# Revit family: Skylight_Velux-Sun_Tunnels-TMC-14in
name_source: partatom
category: Specialty Equipment
revit_build: Autodesk Revit 2015 (Build: 20140606_1530(x64)
units: mm (PartAtom-declared; Revit-internal decimal feet)

## types (1)
- TMC - 14"
    Assembly Code = B3020110
    BIMobject category = Skylights
    BIMobject category code = windows-skylights
    BIMobject main category = Windows
    BIMobject main category code = windows
    Brand url = http://www.veluxusa.com
    Default Elevation = 0' - 0"
    Description = Sun Tunnel Skylight
    Design country = United States
    Dome Material = Acrylic or Polycarbonate - Velux - Clear Impact Modified
    Duct Diameter = 1' - 2"
    Duct Material = Metal - Velux - 99% reflective Aluminum, 0.016" - 0.02" thick
    Edition number = 1
    Flashing Length = 2' - 6 1/2"
    Flashing Material = Metal - Velux - G90 Galvanized Sheet
    Flashing Radius High = 0' - 8 11/16"
    Flashing Radius Low = 0' - 10 9/32"
    Flashing Width = 2' - 5"
    Frame Material = Metal - Velux - G90 Galvanized Sheet
    Installation instructions = http://dd1.domwebx.com
    Manufacturer = VELUX
    Manufacturer name = VELUX US
    Masterformat 2014 Code = 08 62 23
    Masterformat 2014 Description = Tubular Skylights
    Model = TMC 014
    Nominal height = 0' - 0"
    Nominal width = 0' - 0"
    OmniClass Code = 23-17 17 13 21
    OmniClass Description = Tubular Skylights
    Performance Data = http://www.veluxusa.com
    Product Documentation Link = http://www.veluxusa.com
    Product Guid = fd703e04-0772-4454-8332-72b4c6e9ed5e
    Product Page URL = http://www.veluxusa.com
    Product SKU = velux-skylight-tmc
    Product certification = http://www.veluxusa.com
    Product data url = https://bimobject.com
    Product family = Windows
    Product group = Skylights
    Product url = http://www.veluxusa.com
    QR code = http://bimobject.com
    Rough Width = 1' - 2 1/2"
    Technical description = http://dd1.domwebx.com
    UNSPSC Code = 30171803
    URL = http://www.veluxusa.com
    Uniclass 1.4 Code = L4145
    Uniclass 1.4 Description = Skylights
    Uniclass 2015 Code = Pr_30_59_72_77
    Uniclass 2015 Name = Skylights
    Void R1 = 0' - 8 21/32"
    Void R2 = 0' - 10 1/4"
    Weight Net (Kg) = 0
    Width = 1' - 5 9/16"
    Width (Nominal) = 1' - 2"

## geometry (parser evidence)
native form markers: Sweep x6
no freeform markers — native parametric forms only
